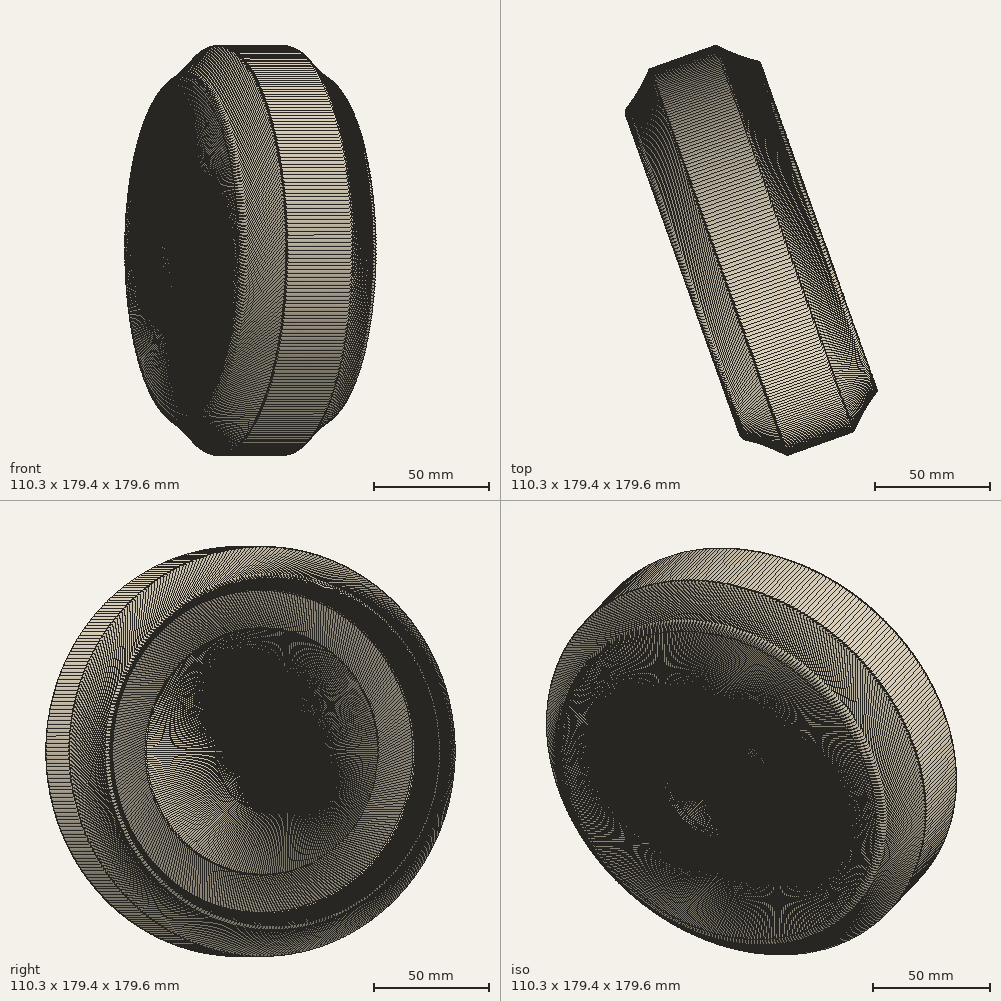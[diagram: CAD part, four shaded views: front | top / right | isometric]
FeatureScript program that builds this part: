
annotation { "Feature Type Name" : "Feature", "Feature Type Description" : "" }
export const myFeature = defineFeature(function(context is Context, id is Id, definition is map)
    precondition{}
    {
        {
            var Q0;
            Q0=qCreatedBy(makeId("Top.planeOp"),FACE);
            var sketch = newSketch(context, id + "F0", { "sketchPlane" : qUnion([Q0])});
            skCircle(sketch, "E0.cCircle", {"center": v(0, 0) * mm, "radius": 31.66 * mm, "construction": true});
            skLineSegment(sketch, "E0.0", {"start": v(24.13, -20.5) * mm, "end": v(-5.69, -31.14) * mm});
            skLineSegment(sketch, "E0.1", {"start": v(-5.69, -31.14) * mm, "end": v(-29.82, -10.64) * mm});
            skLineSegment(sketch, "E0.2", {"start": v(-29.82, -10.64) * mm, "end": v(-24.13, 20.5) * mm});
            skLineSegment(sketch, "E0.3", {"start": v(-24.13, 20.5) * mm, "end": v(5.69, 31.14) * mm});
            skLineSegment(sketch, "E0.4", {"start": v(5.69, 31.14) * mm, "end": v(29.82, 10.64) * mm});
            skLineSegment(sketch, "E0.5", {"start": v(29.82, 10.64) * mm, "end": v(24.13, -20.5) * mm});
            skSolve(sketch);
        }
        {
            var Q0;
            Q0=makeQuery(id+"F0.imprint","IMPRINT",FACE,{"disambiguationData":[TD([[makeQuery(id+"F0.imprint","IMPRINT",EDGE,{"derivedFrom":sQuery(id+"F0.wireOp",EDGE,"E0.0")}),-1.0]])]});
            extrude(context, id + "F1", {"entities" : qUnion([Q0]), "endBound" : BoundingType.SYMMETRIC, "depth" : 76.2 * mm, "offsetDistance" : 25.4 * mm});
        }
        {
            var Q0;
            Q0=makeQuery(id+"F1.opExtrude","SWEPT_FACE",FACE,{"disambiguationData":[OSD([sQuery(id+"F0.wireOp",EDGE,"E0.1")])]});
            var Q1;
            Q1=makeQuery(id+"F1.opExtrude","SWEPT_FACE",FACE,{"disambiguationData":[OSD([sQuery(id+"F0.wireOp",EDGE,"E0.0")])]});
            var Q2;
            Q2=makeQuery(id+"F1.opExtrude","SWEPT_FACE",FACE,{"disambiguationData":[OSD([sQuery(id+"F0.wireOp",EDGE,"E0.5")])]});
            var Q3;
            Q3=makeQuery(id+"F1.opExtrude","SWEPT_FACE",FACE,{"disambiguationData":[OSD([sQuery(id+"F0.wireOp",EDGE,"E0.4")])]});
            var Q4;
            Q4=makeQuery(id+"F1.opExtrude","SWEPT_FACE",FACE,{"disambiguationData":[OSD([sQuery(id+"F0.wireOp",EDGE,"E0.3")])]});
            var Q5;
            Q5=makeQuery(id+"F1.opExtrude","SWEPT_BODY",BODY,{"disambiguationData":[OSD([sQuery(id+"F0.wireOp",EDGE,"E0.0"),sQuery(id+"F0.wireOp",EDGE,"E0.1"),sQuery(id+"F0.wireOp",EDGE,"E0.2"),sQuery(id+"F0.wireOp",EDGE,"E0.3"),sQuery(id+"F0.wireOp",EDGE,"E0.4"),sQuery(id+"F0.wireOp",EDGE,"E0.5")])]});
            shell(context, id + "F2", {"entities" : qUnion([Q0, Q1, Q2, Q3, Q4]), "parts" : qUnion([Q5]), "thickness" : 2.54 * mm});
        }
        {
            var Q0;
            Q0=qCreatedBy(makeId("Top.planeOp"),FACE);
            var sketch = newSketch(context, id + "F3", { "sketchPlane" : qUnion([Q0])});
            skCircle(sketch, "E1", {"center": v(0, 0) * mm, "radius": 14.14 * mm});
            skSolve(sketch);
        }
        {
            var Q0;
            Q0=makeQuery(id+"F3.imprint","IMPRINT",FACE,{"disambiguationData":[TD([[makeQuery(id+"F3.imprint","IMPRINT",EDGE,{"derivedFrom":sQuery(id+"F3.wireOp",EDGE,"E1")}),1.0]])]});
            var Q1;
            {var subQ0=sQuery(id+"F0.wireOp",EDGE,"E0.5");var subQ1=sQuery(id+"F0.wireOp",EDGE,"E0.4");var subQ2=sQuery(id+"F0.wireOp",EDGE,"E0.3");var subQ3=sQuery(id+"F0.wireOp",EDGE,"E0.2");var subQ4=sQuery(id+"F0.wireOp",EDGE,"E0.1");var subQ5=sQuery(id+"F0.wireOp",EDGE,"E0.0");Q1=makeQuery(id+"F2.opShell","OFFSET_FACE",FACE,{"disambiguationData":[OSD([subQ5,subQ4,subQ3,subQ2,subQ1,subQ0]),TDD([makeQuery(id+"F1.opExtrude","CAP_FACE",FACE,{"disambiguationData":[OSD([subQ5,subQ4,subQ3,subQ2,subQ1,subQ0])],"isStart":false})])]});}
            var Q2;
            {var subQ0=sQuery(id+"F0.wireOp",EDGE,"E0.5");var subQ1=sQuery(id+"F0.wireOp",EDGE,"E0.4");var subQ2=sQuery(id+"F0.wireOp",EDGE,"E0.3");var subQ3=sQuery(id+"F0.wireOp",EDGE,"E0.2");var subQ4=sQuery(id+"F0.wireOp",EDGE,"E0.1");var subQ5=sQuery(id+"F0.wireOp",EDGE,"E0.0");Q2=makeQuery(id+"F2.opShell","OFFSET_FACE",FACE,{"disambiguationData":[OSD([subQ5,subQ4,subQ3,subQ2,subQ1,subQ0]),TDD([makeQuery(id+"F1.opExtrude","CAP_FACE",FACE,{"disambiguationData":[OSD([subQ5,subQ4,subQ3,subQ2,subQ1,subQ0])],"isStart":true})])]});}
            extrude(context, id + "F4", {"entities" : qUnion([Q0]), "operationType" : NewBodyOperationType.ADD, "endBound" : BoundingType.UP_TO_SURFACE, "depth" : 76.2 * mm, "endBoundEntityFace" : qUnion([Q1]), "offsetDistance" : 25.4 * mm, "hasSecondDirection" : true, "secondDirectionBound" : SecondDirectionBoundingType.UP_TO_SURFACE, "secondDirectionOppositeDirection" : true, "secondDirectionDepth" : 25.4 * mm, "secondDirectionBoundEntityFace" : qUnion([Q2])});
        }
        {
            var Q0;
            Q0=makeQuery(id+"F4.opExtrude","SWEPT_FACE",FACE,{"disambiguationData":[OSD([sQuery(id+"F3.wireOp",EDGE,"E1")])]});
            chamfer(context, id + "F5", {"entities" : qUnion([Q0]), "width" : 5.08 * mm, "tangentPropagation" : true});
        }
        {
            var Q0;
            Q0=makeQuery(id+"F1.opExtrude","CAP_FACE",FACE,{"disambiguationData":[OSD([sQuery(id+"F0.wireOp",EDGE,"E0.0"),sQuery(id+"F0.wireOp",EDGE,"E0.1"),sQuery(id+"F0.wireOp",EDGE,"E0.2"),sQuery(id+"F0.wireOp",EDGE,"E0.3"),sQuery(id+"F0.wireOp",EDGE,"E0.4"),sQuery(id+"F0.wireOp",EDGE,"E0.5")])],"isStart":false});
            var Q1;
            Q1=makeQuery(id+"F1.opExtrude","CAP_FACE",FACE,{"disambiguationData":[OSD([sQuery(id+"F0.wireOp",EDGE,"E0.0"),sQuery(id+"F0.wireOp",EDGE,"E0.1"),sQuery(id+"F0.wireOp",EDGE,"E0.2"),sQuery(id+"F0.wireOp",EDGE,"E0.3"),sQuery(id+"F0.wireOp",EDGE,"E0.4"),sQuery(id+"F0.wireOp",EDGE,"E0.5")])],"isStart":true});
            fillet(context, id + "F6", {"entities" : qUnion([Q0, Q1]), "radius" : 5.08 * mm, "tangentPropagation" : true, "allowEdgeOverflow" : false});
        }
        {
            var Q0;
            Q0=makeQuery(id+"F1.opExtrude","SWEPT_BODY",BODY,{"disambiguationData":[OSD([sQuery(id+"F0.wireOp",EDGE,"E0.0"),sQuery(id+"F0.wireOp",EDGE,"E0.1"),sQuery(id+"F0.wireOp",EDGE,"E0.2"),sQuery(id+"F0.wireOp",EDGE,"E0.3"),sQuery(id+"F0.wireOp",EDGE,"E0.4"),sQuery(id+"F0.wireOp",EDGE,"E0.5")])]});
            var Q1;
            {var subQ0=sQuery(id+"F0.wireOp",EDGE,"E0.5");var subQ1=sQuery(id+"F0.wireOp",EDGE,"E0.4");var subQ2=sQuery(id+"F0.wireOp",EDGE,"E0.3");var subQ3=sQuery(id+"F0.wireOp",EDGE,"E0.2");var subQ4=sQuery(id+"F0.wireOp",EDGE,"E0.1");var subQ5=sQuery(id+"F0.wireOp",EDGE,"E0.0");Q1=makeQuery(id+"F6.opFillet","BLEND_EDGE",EDGE,{"blendedFrom":[makeQuery(id+"F1.opExtrude","CAP_EDGE",EDGE,{"disambiguationData":[OSD([subQ5])],"isStart":true}),makeQuery(id+"F2.opShell","OFFSET_FACE",FACE,{"disambiguationData":[OSD([subQ5,subQ4,subQ3,subQ2,subQ1,subQ0]),TDD([makeQuery(id+"F1.opExtrude","CAP_FACE",FACE,{"disambiguationData":[OSD([subQ5,subQ4,subQ3,subQ2,subQ1,subQ0])],"isStart":true})])]})],"blendedInto":[makeQuery(id+"F2.opShell","OFFSET_FACE",FACE,{"disambiguationData":[OSD([subQ5,subQ4,subQ3,subQ2,subQ1,subQ0]),TDD([makeQuery(id+"F1.opExtrude","CAP_FACE",FACE,{"disambiguationData":[OSD([subQ5,subQ4,subQ3,subQ2,subQ1,subQ0])],"isStart":true})])]})]});}
            circularPattern(context, id + "F7", {"entities" : qUnion([Q0]), "axis" : qUnion([Q1]), "angle" : 360 * degree, "instanceCount" : 333, "equalSpace" : true});
        }
    });
